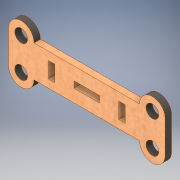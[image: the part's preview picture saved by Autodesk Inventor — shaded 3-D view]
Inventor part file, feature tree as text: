
AUTODESK INVENTOR PART (.ipt)
format: ipt  version: 2019 (Build 230136000, 136)  size: 160,256 bytes
history: native  units: mm
features: other x1, extrude x1, sketch x1
ambient origin geometry x8: Origin, YZ Plane, XZ Plane, XY Plane, X Axis, Y Axis, Z Axis, Center Point
bodies: Body1 (feature_tree)
feature tree (3):
  other  "Твердое тело1"
  extrude  "Выдавливание1"  Depth=8.0mm
  sketch  "Эскиз1"
